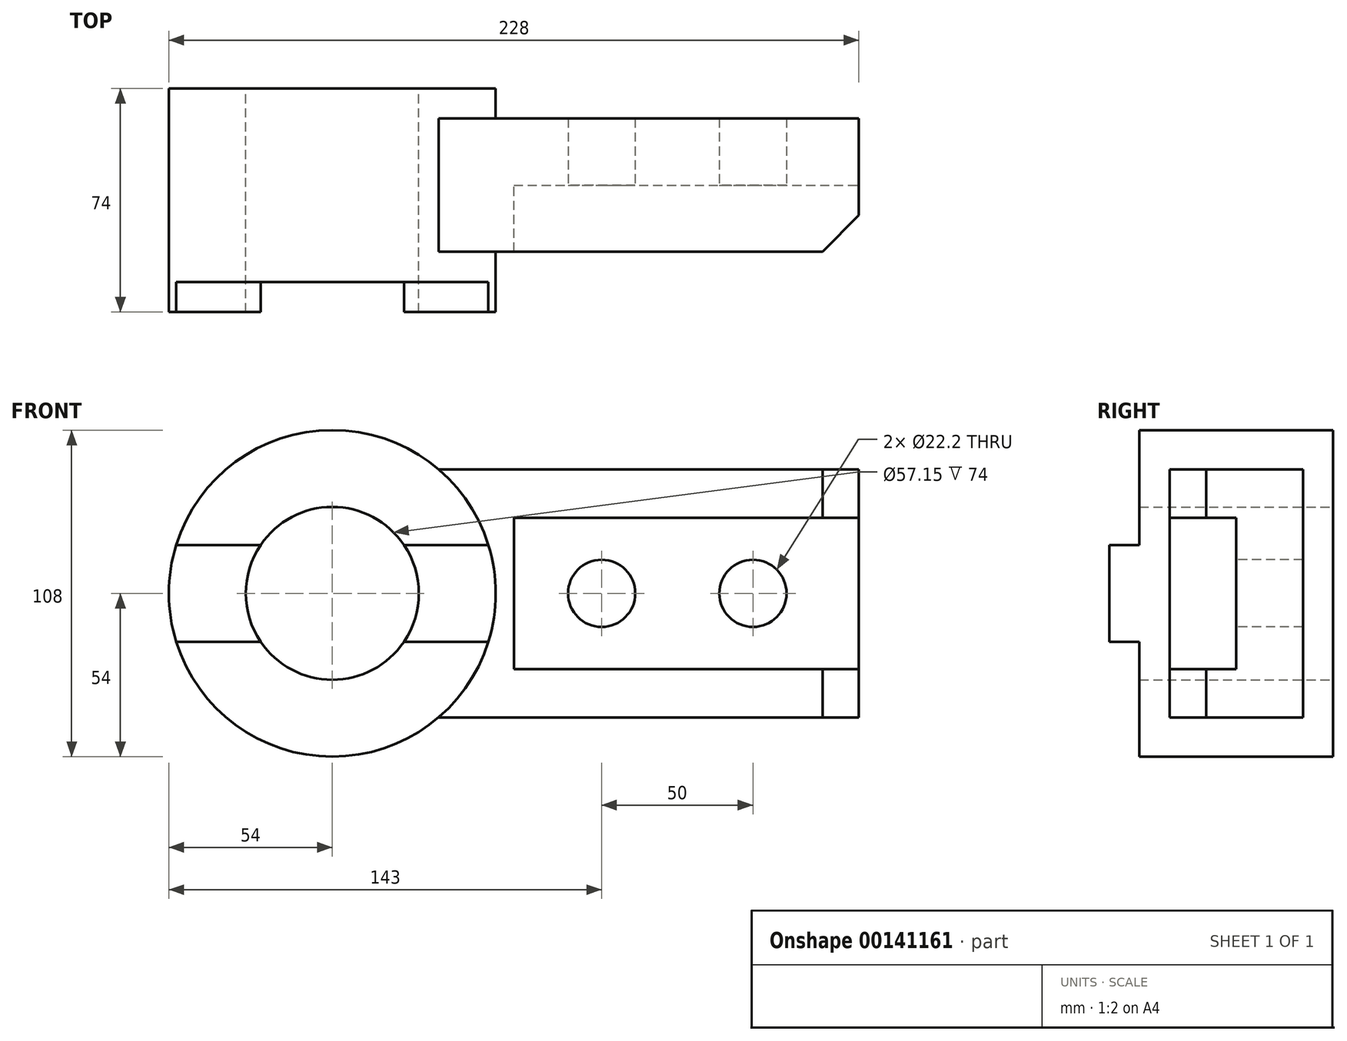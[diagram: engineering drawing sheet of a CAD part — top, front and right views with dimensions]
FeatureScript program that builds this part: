
annotation { "Feature Type Name" : "Feature", "Feature Type Description" : "" }
export const myFeature = defineFeature(function(context is Context, id is Id, definition is map)
    precondition{}
    {
        {
            var Q0;
            Q0=qCreatedBy(makeId("Front.planeOp"),FACE);
            var sketch = newSketch(context, id + "F0", { "sketchPlane" : qUnion([Q0])});
            skCircle(sketch, "E0", {"center": v(0, 0) * mm, "radius": 54 * mm});
            skLineSegment(sketch, "E1", {"start": v(35.14, 41) * mm, "end": v(174, 41) * mm});
            skLineSegment(sketch, "E2", {"start": v(174, 41) * mm, "end": v(174, -41) * mm});
            skLineSegment(sketch, "E3", {"start": v(174, -41) * mm, "end": v(35.14, -41) * mm});
            skCircle(sketch, "E4", {"center": v(0, 0) * mm, "radius": 28.57 * mm});
            skSolve(sketch);
        }
        {
            var Q0;
            {var subQ0=sQuery(id+"F0.wireOp",EDGE,"E1");Q0=makeQuery(id+"F0.imprint","IMPRINT",FACE,{"disambiguationData":[TD([[makeQuery(id+"F0.imprint","IMPRINT",EDGE,{"derivedFrom":subQ0}),-1.0]])]});}
            extrude(context, id + "F1", {"entities" : qUnion([Q0]), "endBound" : BoundingType.SYMMETRIC, "depth" : 44 * mm});
        }
        {
            var Q0;
            Q0=makeQuery(id+"F0.imprint","IMPRINT",FACE,{"disambiguationData":[TD([[makeQuery(id+"F0.imprint","IMPRINT",EDGE,{"derivedFrom":sQuery(id+"F0.wireOp",EDGE,"E4")}),-1.0]])]});
            var Q1;
            Q1=makeQuery(id+"F0.imprint","IMPRINT",FACE,{"disambiguationData":[TD([[makeQuery(id+"F0.imprint","IMPRINT",EDGE,{"derivedFrom":sQuery(id+"F0.wireOp",EDGE,"E4")}),1.0]])]});
            extrude(context, id + "F2", {"entities" : qUnion([Q0, Q1]), "operationType" : NewBodyOperationType.ADD, "endBound" : BoundingType.SYMMETRIC, "depth" : 64 * mm});
        }
        {
            var Q0;
            Q0=makeQuery(id+"F1.opExtrude","SWEPT_FACE",FACE,{"disambiguationData":[OSD([sQuery(id+"F0.wireOp",EDGE,"E2")])]});
            var sketch = newSketch(context, id + "F3", { "sketchPlane" : qUnion([Q0])});
            skLineSegment(sketch, "E5.bottom", {"start": v(-22, 25) * mm, "end": v(0, 25) * mm});
            skLineSegment(sketch, "E5.top", {"start": v(-22, -25) * mm, "end": v(0, -25) * mm});
            skLineSegment(sketch, "E5.left", {"start": v(-22, 25) * mm, "end": v(-22, -25) * mm});
            skLineSegment(sketch, "E5.right", {"start": v(0, 25) * mm, "end": v(0, -25) * mm});
            skSolve(sketch);
        }
        {
            var Q0;
            Q0=makeQuery(id+"F3.imprint","IMPRINT",FACE,{"disambiguationData":[TD([[makeQuery(id+"F3.imprint","IMPRINT",EDGE,{"derivedFrom":sQuery(id+"F3.wireOp",EDGE,"E5.bottom")}),-1.0]])]});
            extrude(context, id + "F4", {"entities" : qUnion([Q0]), "operationType" : NewBodyOperationType.REMOVE, "oppositeDirection" : true, "depth" : 114 * mm});
        }
        {
            var Q0;
            Q0=makeQuery(id+"F4.boolean.opBoolean","COPY",FACE,{"derivedFrom":makeQuery(id+"F4.opExtrude","SWEPT_FACE",FACE,{"disambiguationData":[OSD([sQuery(id+"F3.wireOp",EDGE,"E5.right")])]})});
            var sketch = newSketch(context, id + "F5", { "sketchPlane" : qUnion([Q0])});
            skCircle(sketch, "E6", {"center": v(89, 0) * mm, "radius": 11.1 * mm});
            skCircle(sketch, "E7", {"center": v(139, 0) * mm, "radius": 11.1 * mm});
            skSolve(sketch);
        }
        {
            var Q0;
            Q0=makeQuery(id+"F5.imprint","IMPRINT",FACE,{"disambiguationData":[TD([[makeQuery(id+"F5.imprint","IMPRINT",EDGE,{"derivedFrom":sQuery(id+"F5.wireOp",EDGE,"E7")}),1.0]])]});
            var Q1;
            Q1=makeQuery(id+"F5.imprint","IMPRINT",FACE,{"disambiguationData":[TD([[makeQuery(id+"F5.imprint","IMPRINT",EDGE,{"derivedFrom":sQuery(id+"F5.wireOp",EDGE,"E6")}),1.0]])]});
            extrude(context, id + "F6", {"entities" : qUnion([Q0, Q1]), "operationType" : NewBodyOperationType.REMOVE, "endBound" : BoundingType.THROUGH_ALL, "oppositeDirection" : true, "depth" : 25 * mm});
        }
        {
            var Q0;
            Q0=makeQuery(id+"F2.opExtrude","CAP_FACE",FACE,{"disambiguationData":[OSD([sQuery(id+"F0.wireOp",EDGE,"E0")])],"isStart":false});
            var sketch = newSketch(context, id + "F7", { "sketchPlane" : qUnion([Q0])});
            skCircle(sketch, "E8.0", {"center": v(0, 0) * mm, "radius": 28.57 * mm});
            skCircle(sketch, "E9.0", {"center": v(0, 0) * mm, "radius": 54 * mm});
            skLineSegment(sketch, "E10", {"start": v(-23.68, 16) * mm, "end": v(-51.58, 16) * mm});
            skLineSegment(sketch, "E11", {"start": v(-23.68, -16) * mm, "end": v(-51.58, -16) * mm});
            skLineSegment(sketch, "E12", {"start": v(23.68, -16) * mm, "end": v(51.58, -16) * mm});
            skLineSegment(sketch, "E13", {"start": v(23.68, 16) * mm, "end": v(51.58, 16) * mm});
            skSolve(sketch);
        }
        {
            var Q0;
            {var subQ0=sQuery(id+"F7.wireOp",EDGE,"E10");Q0=makeQuery(id+"F7.imprint","IMPRINT",FACE,{"disambiguationData":[TD([[makeQuery(id+"F7.imprint","IMPRINT",EDGE,{"derivedFrom":subQ0}),1.0]])]});}
            var Q1;
            {var subQ0=sQuery(id+"F7.wireOp",EDGE,"E12");Q1=makeQuery(id+"F7.imprint","IMPRINT",FACE,{"disambiguationData":[TD([[makeQuery(id+"F7.imprint","IMPRINT",EDGE,{"derivedFrom":subQ0}),1.0]])]});}
            extrude(context, id + "F8", {"entities" : qUnion([Q0, Q1]), "operationType" : NewBodyOperationType.ADD, "depth" : 10 * mm});
        }
        {
            var Q0;
            {var subQ0=sQuery(id+"F7.wireOp",EDGE,"E8.0");var subQ1=makeQuery(id+"F7.imprint","INTERSECT",VERTEX,{"derivedFrom":[subQ0,sQuery(id+"F7.wireOp",EDGE,"E12")]});Q0=makeQuery(id+"F7.imprint","IMPRINT",FACE,{"disambiguationData":[TD([[makeQuery(id+"F7.imprint","IMPRINT",EDGE,{"disambiguationData":[TD([[subQ1,-1.0]])],"derivedFrom":subQ0}),1.0]])]});}
            extrude(context, id + "F9", {"entities" : qUnion([Q0]), "operationType" : NewBodyOperationType.REMOVE, "endBound" : BoundingType.THROUGH_ALL, "oppositeDirection" : true, "depth" : 25 * mm});
        }
        {
            var Q0;
            {var subQ0=sQuery(id+"F0.wireOp",EDGE,"E2");var subQ1=sQuery(id+"F0.wireOp",EDGE,"E1");Q0=makeQuery(id+"F4.boolean.opBoolean","SPLIT",EDGE,{"disambiguationData":[TD([makeQuery(id+"F1.opExtrude","SWEPT_FACE",FACE,{"disambiguationData":[OSD([subQ1])]})])],"derivedFrom":makeQuery(id+"F1.opExtrude","CAP_EDGE",EDGE,{"disambiguationData":[OSD([subQ0])],"isStart":false})});}
            var Q1;
            {var subQ0=sQuery(id+"F0.wireOp",EDGE,"E3");var subQ1=sQuery(id+"F0.wireOp",EDGE,"E2");Q1=makeQuery(id+"F4.boolean.opBoolean","SPLIT",EDGE,{"disambiguationData":[TD([makeQuery(id+"F1.opExtrude","SWEPT_FACE",FACE,{"disambiguationData":[OSD([subQ0])]})])],"derivedFrom":makeQuery(id+"F1.opExtrude","CAP_EDGE",EDGE,{"disambiguationData":[OSD([subQ1])],"isStart":false})});}
            chamfer(context, id + "F10", {"entities" : qUnion([Q0, Q1]), "chamferType" : ChamferType.OFFSET_ANGLE, "width" : 12 * mm, "oppositeDirection" : false, "angle" : 45 * degree, "tangentPropagation" : true});
        }
    });
